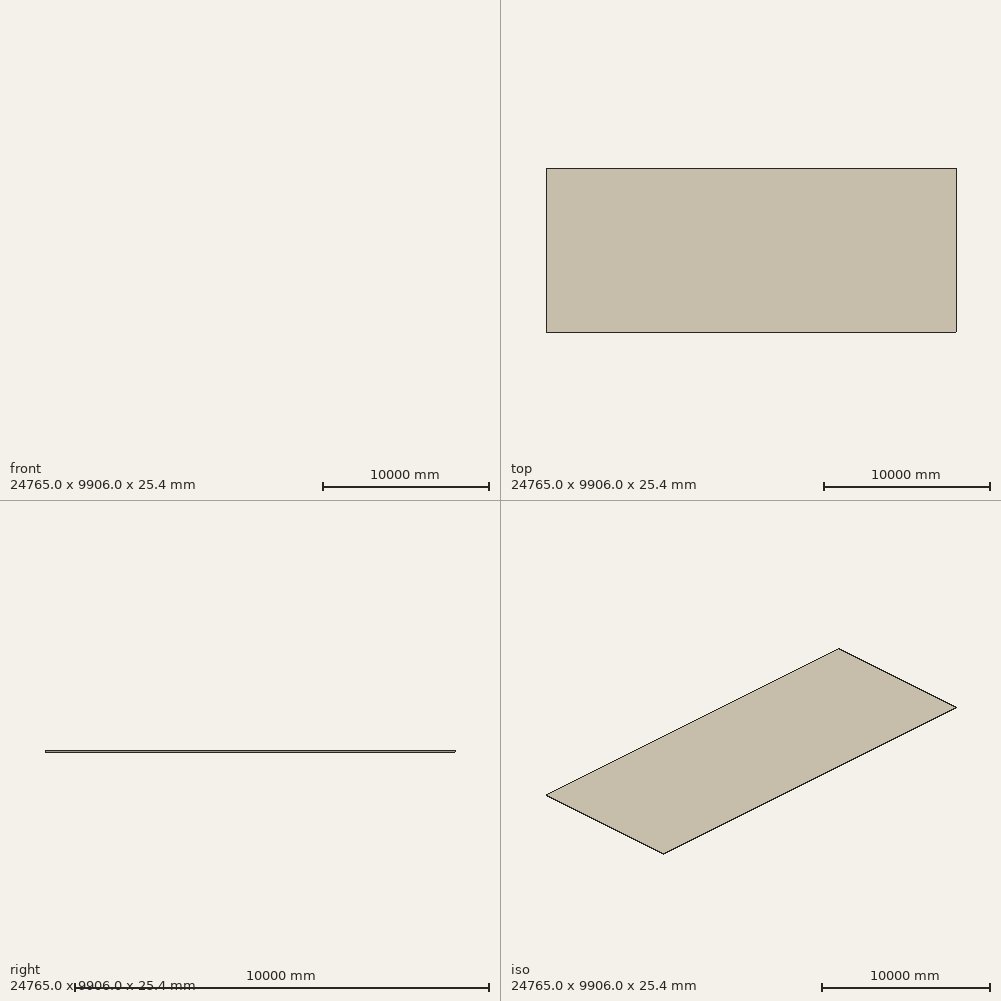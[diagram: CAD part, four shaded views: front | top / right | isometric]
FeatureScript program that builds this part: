
annotation { "Feature Type Name" : "Feature", "Feature Type Description" : "" }
export const myFeature = defineFeature(function(context is Context, id is Id, definition is map)
    precondition{}
    {
        {
            var Q0;
            Q0=qCreatedBy(makeId("Top.planeOp"),FACE);
            var sketch = newSketch(context, id + "F0", { "sketchPlane" : qUnion([Q0])});
            skLineSegment(sketch, "E0.bottom", {"start": v(0, 0) * mm, "end": v(24765, 0) * mm});
            skLineSegment(sketch, "E0.top", {"start": v(0, 9906) * mm, "end": v(24765, 9906) * mm});
            skLineSegment(sketch, "E0.left", {"start": v(0, 0) * mm, "end": v(0, 9906) * mm});
            skLineSegment(sketch, "E0.right", {"start": v(24765, 0) * mm, "end": v(24765, 9906) * mm});
            skSolve(sketch);
        }
        {
            var Q0;
            Q0=makeQuery(id+"F0.imprint","IMPRINT",FACE,{"disambiguationData":[TD([[makeQuery(id+"F0.imprint","IMPRINT",EDGE,{"derivedFrom":sQuery(id+"F0.wireOp",EDGE,"E0.bottom")}),1.0]])]});
            extrude(context, id + "F1", {"entities" : qUnion([Q0]), "depth" : 25.4 * mm});
        }
    });
